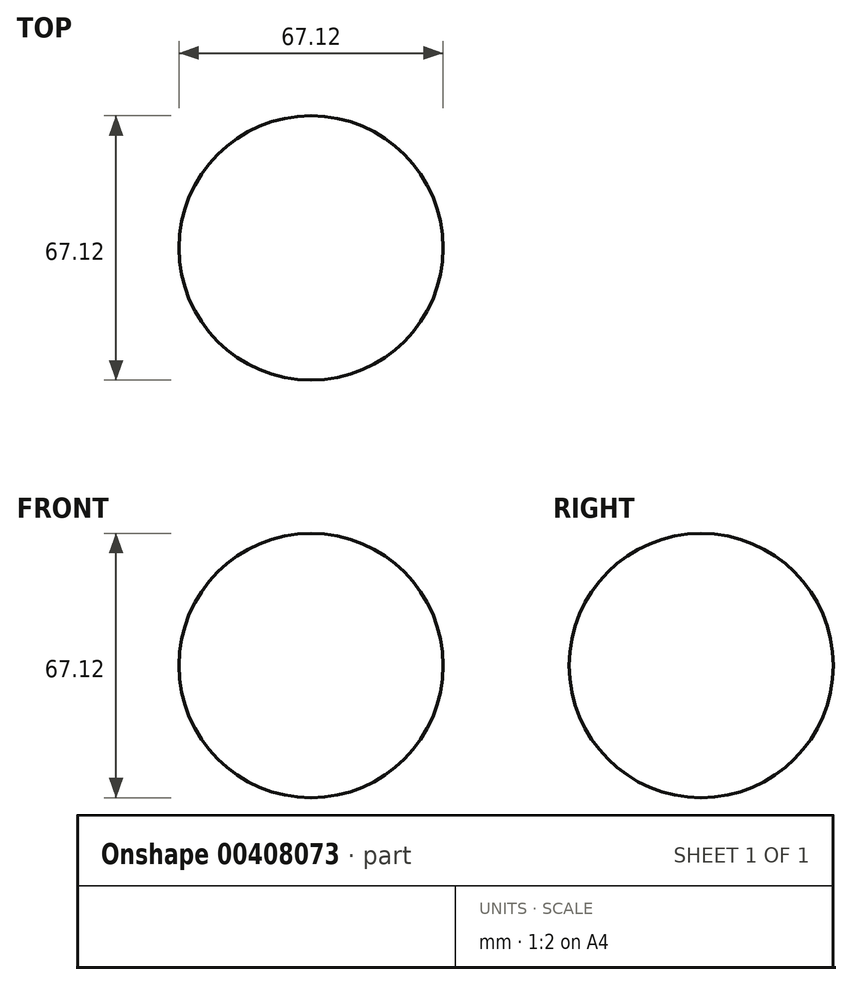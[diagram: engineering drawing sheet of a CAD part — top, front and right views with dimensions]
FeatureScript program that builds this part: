
annotation { "Feature Type Name" : "Feature", "Feature Type Description" : "" }
export const myFeature = defineFeature(function(context is Context, id is Id, definition is map)
    precondition{}
    {
        {
            var Q0;
            Q0=qCreatedBy(makeId("Top.planeOp"),FACE);
            var sketch = newSketch(context, id + "F0", { "sketchPlane" : qUnion([Q0])});
            skLineSegment(sketch, "E0", {"start": v(0, 54.77) * mm, "end": v(0, -20.95) * mm});
            skArc(sketch, "E1", {"start": v(0, -12.62) * mm, "mid": v(33.56, 20.94) * mm, "end": v(0, 54.5) * mm});
            skSolve(sketch);
        }
        {
            var Q0;
            Q0=sQuery(id+"F0.wireOp",EDGE,"E1");
            var Q1;
            Q1=sQuery(id+"F0.wireOp",EDGE,"E0");
            revolve(context, id + "F1", {"bodyType" : ToolBodyType.SURFACE, "surfaceEntities" : qUnion([Q0]), "axis" : qUnion([Q1]), "revolveType" : RevolveType.FULL});
        }
    });
